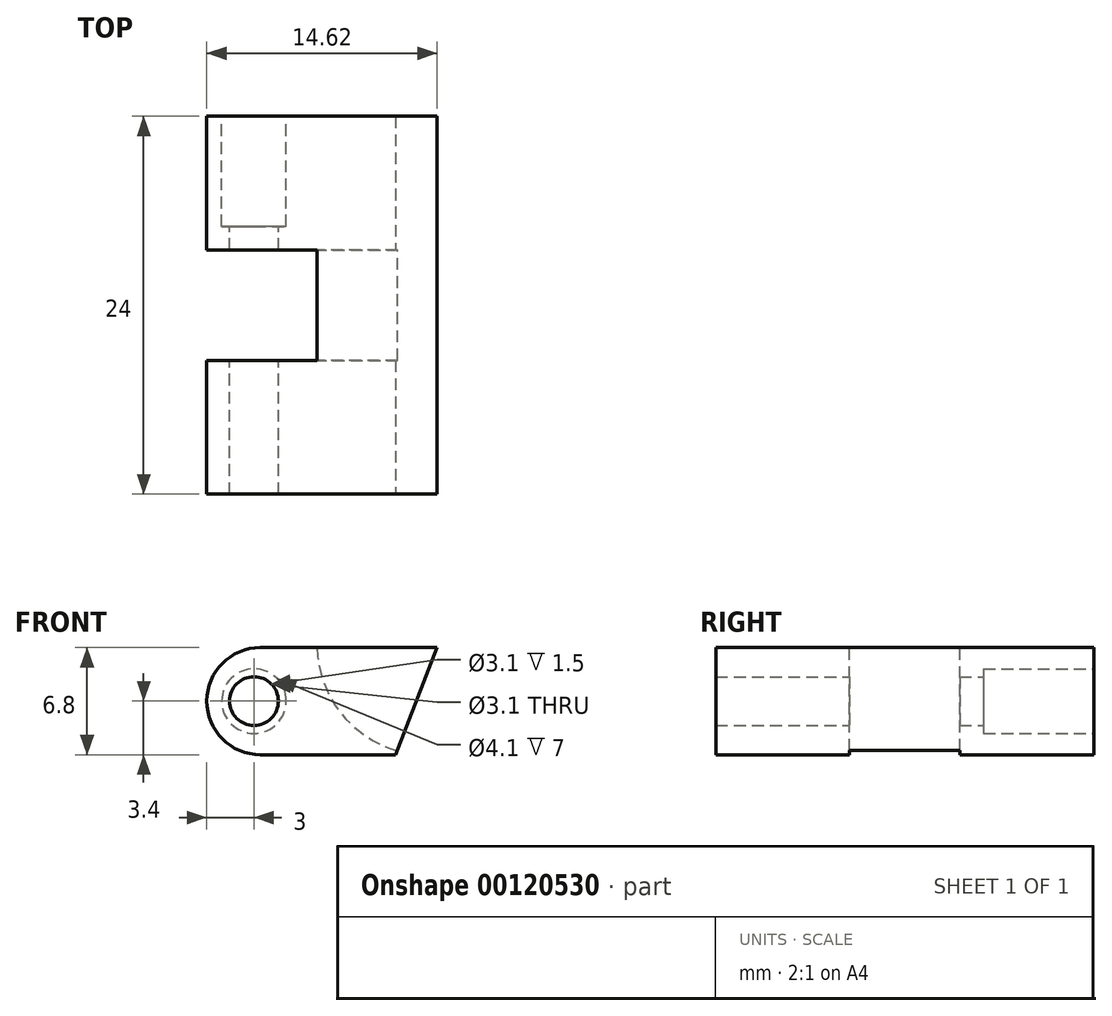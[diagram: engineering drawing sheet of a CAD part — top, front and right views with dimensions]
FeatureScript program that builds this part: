
annotation { "Feature Type Name" : "Feature", "Feature Type Description" : "" }
export const myFeature = defineFeature(function(context is Context, id is Id, definition is map)
    precondition{}
    {
        {
            var Q0;
            Q0=qCreatedBy(makeId("Top.planeOp"),FACE);
            var sketch = newSketch(context, id + "F0", { "sketchPlane" : qUnion([Q0])});
            skLineSegment(sketch, "E0", {"start": v(0, -12) * mm, "end": v(-2, -12) * mm});
            skLineSegment(sketch, "E1", {"start": v(-2, -12) * mm, "end": v(-9, -12) * mm});
            skLineSegment(sketch, "E2", {"start": v(-9, -12) * mm, "end": v(-9, -3.5) * mm});
            skLineSegment(sketch, "E3", {"start": v(-9, -3.5) * mm, "end": v(-2, -3.5) * mm});
            skPoint(sketch, "E4", {"position": v(-2, 0) * mm});
            skLineSegment(sketch, "E5.MirrorCS", {"start": v(-9, 12) * mm, "end": v(-9, 3.5) * mm});
            skLineSegment(sketch, "E6.MirrorCS", {"start": v(-9, 3.5) * mm, "end": v(-2, 3.5) * mm});
            skLineSegment(sketch, "E7.MirrorCS", {"start": v(0, 12) * mm, "end": v(-2, 12) * mm});
            skLineSegment(sketch, "E8.MirrorCS", {"start": v(-2, 12) * mm, "end": v(-9, 12) * mm});
            skLineSegment(sketch, "E9", {"start": v(0, -12) * mm, "end": v(0, 12) * mm});
            skPoint(sketch, "E10.orphan", {"position": v(0, 23.14) * mm});
            skPoint(sketch, "E11.orphan", {"position": v(0, -34.54) * mm});
            skPoint(sketch, "E12.MirrorCS.end.orphan", {"position": v(0, -19.04) * mm});
            skPoint(sketch, "E13.start.orphan", {"position": v(2.04, -21.24) * mm});
            skPoint(sketch, "E14.orphan", {"position": v(24.85, 0) * mm});
            skLineSegment(sketch, "E15.bottom", {"start": v(0, -12) * mm, "end": v(8, -12) * mm});
            skLineSegment(sketch, "E15.top", {"start": v(0, 12) * mm, "end": v(8, 12) * mm});
            skLineSegment(sketch, "E15.right", {"start": v(8, -12) * mm, "end": v(8, 12) * mm});
            skLineSegment(sketch, "E16", {"start": v(-2, -3.5) * mm, "end": v(-2, 3.5) * mm});
            skSolve(sketch);
        }
        {
            var Q0;
            Q0=makeQuery(id+"F0.imprint","IMPRINT",FACE,{"disambiguationData":[TD([[makeQuery(id+"F0.imprint","IMPRINT",EDGE,{"derivedFrom":sQuery(id+"F0.wireOp",EDGE,"zT8ULMTL-c5zF-14Nq-p09k-rvLnDzIjeo5f")}),-1.0]])]});
            var Q1;
            {var subQ1=sQuery(id+"F0.wireOp",EDGE,"E1");Q1=makeQuery(id+"F0.imprint","IMPRINT",FACE,{"disambiguationData":[TD([[makeQuery(id+"F0.imprint","IMPRINT",EDGE,{"derivedFrom":subQ1}),-1.0]])]});}
            var Q2;
            {var subQ0=sQuery(id+"F0.wireOp",EDGE,"E13");Q2=makeQuery(id+"F0.imprint","IMPRINT",FACE,{"disambiguationData":[TD([[makeQuery(id+"F0.imprint","IMPRINT",EDGE,{"derivedFrom":subQ0}),1.0]])]});}
            extrude(context, id + "F1", {"entities" : qUnion([Q0, Q1, Q2]), "depth" : 6.8 * mm});
        }
        {
            var Q0;
            Q0=makeQuery(id+"F1.opExtrude","CAP_EDGE",EDGE,{"disambiguationData":[OSD([sQuery(id+"F0.wireOp",EDGE,"E5.MirrorCS")])],"isStart":false});
            var Q1;
            Q1=makeQuery(id+"F1.opExtrude","CAP_EDGE",EDGE,{"disambiguationData":[OSD([sQuery(id+"F0.wireOp",EDGE,"E5.MirrorCS")])],"isStart":true});
            var Q2;
            Q2=makeQuery(id+"F1.opExtrude","CAP_EDGE",EDGE,{"disambiguationData":[OSD([sQuery(id+"F0.wireOp",EDGE,"E2")])],"isStart":true});
            var Q3;
            Q3=makeQuery(id+"F1.opExtrude","CAP_EDGE",EDGE,{"disambiguationData":[OSD([sQuery(id+"F0.wireOp",EDGE,"E2")])],"isStart":false});
            var Q4;
            Q4=makeQuery(id+"F1.opExtrude","CAP_EDGE",EDGE,{"disambiguationData":[OSD([sQuery(id+"F0.wireOp",EDGE,"r5UAIrGx-vygU-qZuc-aVMr-Vnal8U8UbUhX"),sQuery(id+"F0.wireOp",EDGE,"a6777493-8ee2-40ea-9bb6-514de34b343c0.MirrorCS")])],"isStart":true});
            var Q5;
            Q5=makeQuery(id+"F1.opExtrude","CAP_EDGE",EDGE,{"disambiguationData":[OSD([sQuery(id+"F0.wireOp",EDGE,"r5UAIrGx-vygU-qZuc-aVMr-Vnal8U8UbUhX"),sQuery(id+"F0.wireOp",EDGE,"a6777493-8ee2-40ea-9bb6-514de34b343c0.MirrorCS")])],"isStart":false});
            fillet(context, id + "F2", {"entities" : qUnion([Q0, Q1, Q2, Q3, Q4, Q5]), "radius" : 6.8 * mm / 2, "tangentPropagation" : true, "allowEdgeOverflow" : false});
        }
        {
            var Q0;
            Q0=makeQuery(id+"F1.opExtrude","SWEPT_FACE",FACE,{"disambiguationData":[OSD([sQuery(id+"F0.wireOp",EDGE,"E8.MirrorCS")])]});
            var sketch = newSketch(context, id + "F3", { "sketchPlane" : qUnion([Q0])});
            skLineSegment(sketch, "E17", {"start": v(5.6, 0) * mm, "end": v(5.6, 6.8) * mm, "construction": true});
            skPoint(sketch, "E18", {"position": v(6, 3.4) * mm});
            skCircle(sketch, "E19", {"center": v(6, 3.4) * mm, "radius": 2.05 * mm});
            skCircle(sketch, "E20", {"center": v(6, 3.4) * mm, "radius": 1.55 * mm});
            skLineSegment(sketch, "E21", {"start": v(6, 6.78) * mm, "end": v(6, 0.02) * mm, "construction": true});
            skSolve(sketch);
        }
        {
            var Q0;
            Q0=makeQuery(id+"F3.imprint","IMPRINT",FACE,{"disambiguationData":[TD([[makeQuery(id+"F3.imprint","IMPRINT",EDGE,{"derivedFrom":sQuery(id+"F3.wireOp",EDGE,"E20")}),1.0]])]});
            extrude(context, id + "F4", {"entities" : qUnion([Q0]), "operationType" : NewBodyOperationType.REMOVE, "endBound" : BoundingType.THROUGH_ALL, "oppositeDirection" : true, "depth" : 25 * mm});
        }
        {
            var Q0;
            Q0=makeQuery(id+"F3.imprint","IMPRINT",FACE,{"disambiguationData":[TD([[makeQuery(id+"F3.imprint","IMPRINT",EDGE,{"derivedFrom":sQuery(id+"F3.wireOp",EDGE,"E19")}),1.0]])]});
            extrude(context, id + "F5", {"entities" : qUnion([Q0]), "operationType" : NewBodyOperationType.REMOVE, "oppositeDirection" : true, "depth" : 7 * mm});
        }
        {
            var Q0;
            Q0=makeQuery(id+"F0.imprint","IMPRINT",FACE,{"disambiguationData":[TD([[makeQuery(id+"F0.imprint","IMPRINT",EDGE,{"derivedFrom":sQuery(id+"F0.wireOp",EDGE,"E15.bottom")}),1.0]])]});
            var Q1;
            Q1=makeQuery(id+"F1.opExtrude","CAP_FACE",FACE,{"disambiguationData":[OSD([sQuery(id+"F0.wireOp",EDGE,"E0"),sQuery(id+"F0.wireOp",EDGE,"E1"),sQuery(id+"F0.wireOp",EDGE,"E2"),sQuery(id+"F0.wireOp",EDGE,"E3"),sQuery(id+"F0.wireOp",EDGE,"r5UAIrGx-vygU-qZuc-aVMr-Vnal8U8UbUhX"),sQuery(id+"F0.wireOp",EDGE,"a6777493-8ee2-40ea-9bb6-514de34b343c0.MirrorCS"),sQuery(id+"F0.wireOp",EDGE,"E5.MirrorCS"),sQuery(id+"F0.wireOp",EDGE,"E6.MirrorCS"),sQuery(id+"F0.wireOp",EDGE,"E7.MirrorCS"),sQuery(id+"F0.wireOp",EDGE,"E8.MirrorCS"),sQuery(id+"F0.wireOp",EDGE,"Wm3jARsY-aOFY-taCI-q56u-3gJQePx0DChd")])],"isStart":false});
            extrude(context, id + "F6", {"entities" : qUnion([Q0]), "operationType" : NewBodyOperationType.ADD, "endBound" : BoundingType.UP_TO_SURFACE, "endBoundEntityFace" : qUnion([Q1]), "depth" : 25 * mm, "offsetDistance" : 25 * mm});
        }
        {
            var Q0;
            Q0=makeQuery(id+"F1.opExtrude","CAP_EDGE",EDGE,{"disambiguationData":[OSD([sQuery(id+"F0.wireOp",EDGE,"E16")])],"isStart":true});
            fillet(context, id + "F7", {"entities" : qUnion([Q0]), "radius" : 7 * mm, "tangentPropagation" : true, "allowEdgeOverflow" : false});
        }
        {
            var Q0;
            Q0=makeQuery(id+"F6.opExtrude","CAP_EDGE",EDGE,{"disambiguationData":[OSD([sQuery(id+"F0.wireOp",EDGE,"E15.right")])],"isStart":true});
            chamfer(context, id + "F8", {"entities" : qUnion([Q0]), "chamferType" : ChamferType.TWO_OFFSETS, "width1" : 5 * mm, "oppositeDirection" : false, "width2" : 13 * mm, "tangentPropagation" : true});
        }
    });
